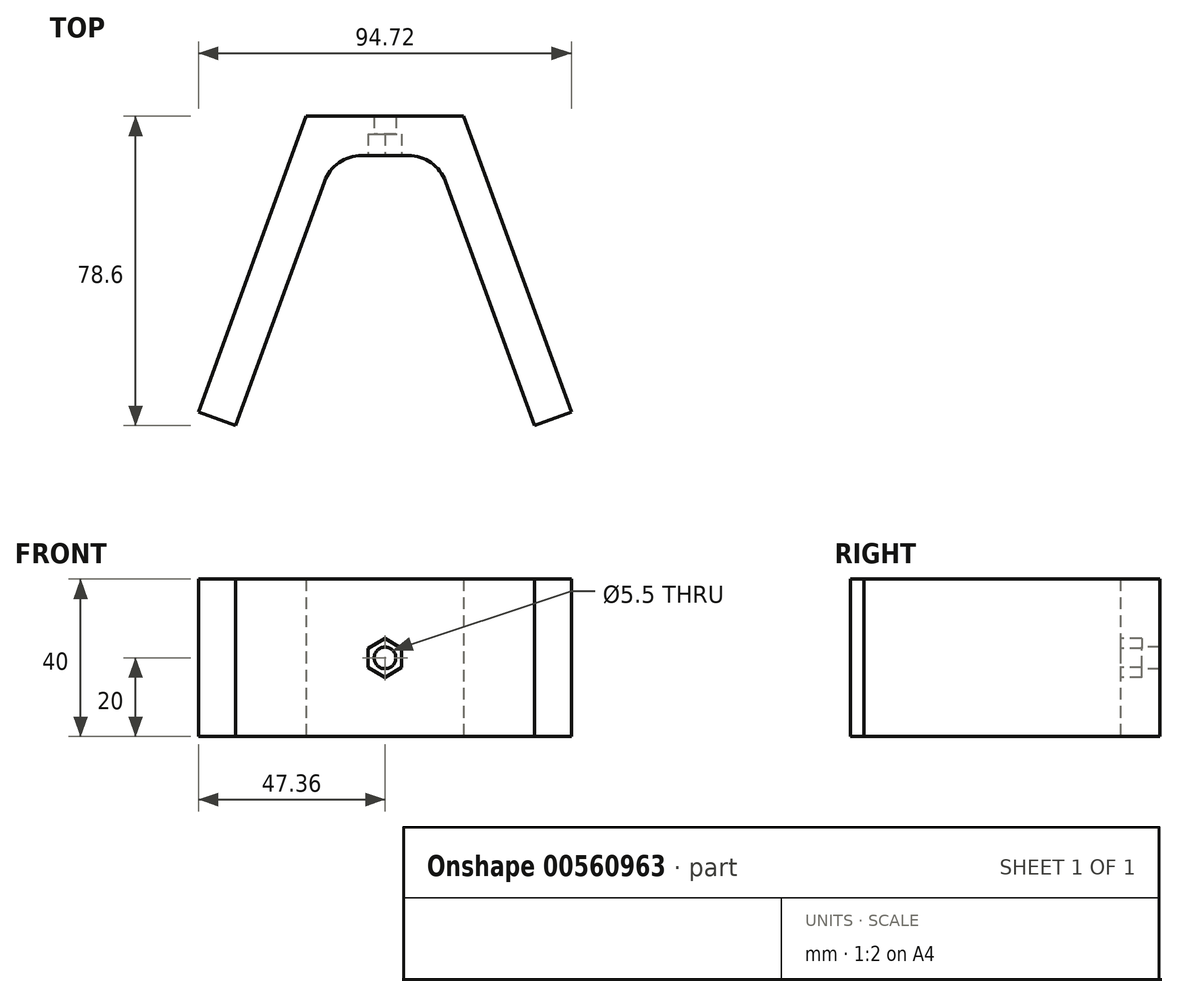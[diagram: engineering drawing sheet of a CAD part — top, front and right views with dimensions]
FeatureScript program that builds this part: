
annotation { "Feature Type Name" : "Feature", "Feature Type Description" : "" }
export const myFeature = defineFeature(function(context is Context, id is Id, definition is map)
    precondition{}
    {
        {
            var Q0;
            Q0=qCreatedBy(makeId("Top.planeOp"),FACE);
            var sketch = newSketch(context, id + "F0", { "sketchPlane" : qUnion([Q0])});
            skLineSegment(sketch, "E0.bottom", {"start": v(-20, 0) * mm, "end": v(0, 0) * mm});
            skLineSegment(sketch, "E0.top", {"start": v(-20, -10) * mm, "end": v(0, -10) * mm});
            skLineSegment(sketch, "E0.left", {"start": v(-20, 0) * mm, "end": v(-20, -10) * mm});
            skLineSegment(sketch, "E0.right", {"start": v(0, 0) * mm, "end": v(0, -10) * mm});
            skLineSegment(sketch, "E1", {"start": v(-20, 0) * mm, "end": v(-47.36, -75.18) * mm});
            skLineSegment(sketch, "E2", {"start": v(-47.36, -75.18) * mm, "end": v(-37.96, -78.6) * mm});
            skLineSegment(sketch, "E3", {"start": v(-37.96, -78.6) * mm, "end": v(-13, -10) * mm});
            skSolve(sketch);
        }
        {
            var Q0;
            Q0=makeQuery(id+"F0.imprint","IMPRINT",FACE,{"disambiguationData":[TD([[makeQuery(id+"F0.imprint","IMPRINT",EDGE,{"derivedFrom":sQuery(id+"F0.wireOp",EDGE,"E0.bottom")}),-1.0]])]});
            var Q1;
            {var subQ0=sQuery(id+"F0.wireOp",EDGE,"E0.left");Q1=makeQuery(id+"F0.imprint","IMPRINT",FACE,{"disambiguationData":[TD([[makeQuery(id+"F0.imprint","IMPRINT",EDGE,{"derivedFrom":subQ0}),-1.0]])]});}
            extrude(context, id + "F1", {"entities" : qUnion([Q0, Q1]), "depth" : 40 * mm, "offsetDistance" : 25 * mm});
        }
        {
            var Q0;
            Q0=makeQuery(id+"F1.opExtrude","SWEPT_BODY",BODY,{"disambiguationData":[OSD([sQuery(id+"F0.wireOp",EDGE,"E0.bottom"),sQuery(id+"F0.wireOp",EDGE,"E0.top"),sQuery(id+"F0.wireOp",EDGE,"E0.right"),sQuery(id+"F0.wireOp",EDGE,"E1"),sQuery(id+"F0.wireOp",EDGE,"E2"),sQuery(id+"F0.wireOp",EDGE,"E3")])]});
            var Q1;
            Q1=qCreatedBy(makeId("Right.planeOp"),FACE);
            mirror(context, id + "F2", {"operationType" : NewBodyOperationType.ADD, "entities" : qUnion([Q0]), "mirrorPlane" : qUnion([Q1])});
        }
        {
            var Q0;
            {var subQ0=makeQuery(id+"F1.opExtrude","SWEPT_FACE",FACE,{"disambiguationData":[OSD([sQuery(id+"F0.wireOp",EDGE,"E0.top")])]});Q0=makeQuery(id+"F2.boolean.opBoolean","MERGE",FACE,{"derivedFrom":[subQ0,makeQuery(id+"F2.opPattern","COPY",FACE,{"derivedFrom":subQ0,"instanceName":"1"})]});}
            var sketch = newSketch(context, id + "F3", { "sketchPlane" : qUnion([Q0])});
            skCircle(sketch, "E4", {"center": v(0, 20) * mm, "radius": 2.75 * mm});
            skPoint(sketch, "E4.centerSnap0", {"position": v(13, 20) * mm});
            skSolve(sketch);
        }
        {
            var Q0;
            Q0=makeQuery(id+"F3.imprint","IMPRINT",FACE,{"disambiguationData":[TD([[makeQuery(id+"F3.imprint","IMPRINT",EDGE,{"derivedFrom":sQuery(id+"F3.wireOp",EDGE,"E4")}),1.0]])]});
            extrude(context, id + "F4", {"entities" : qUnion([Q0]), "operationType" : NewBodyOperationType.REMOVE, "endBound" : BoundingType.UP_TO_NEXT, "oppositeDirection" : true, "depth" : 25 * mm, "offsetDistance" : 25 * mm});
        }
        {
            var Q0;
            {var subQ0=makeQuery(id+"F1.opExtrude","SWEPT_FACE",FACE,{"disambiguationData":[OSD([sQuery(id+"F0.wireOp",EDGE,"E0.top")])]});Q0=makeQuery(id+"F2.boolean.opBoolean","MERGE",FACE,{"derivedFrom":[subQ0,makeQuery(id+"F2.opPattern","COPY",FACE,{"derivedFrom":subQ0,"instanceName":"1"})]});}
            var sketch = newSketch(context, id + "F5", { "sketchPlane" : qUnion([Q0])});
            skCircle(sketch, "E5.cCircle", {"center": v(0, 20) * mm, "radius": 4.25 * mm, "construction": true});
            skLineSegment(sketch, "E5.0", {"start": v(0, 24.9) * mm, "end": v(4.25, 22.45) * mm});
            skLineSegment(sketch, "E5.1", {"start": v(4.25, 22.45) * mm, "end": v(4.25, 17.55) * mm});
            skLineSegment(sketch, "E5.2", {"start": v(4.25, 17.55) * mm, "end": v(0, 15.1) * mm});
            skLineSegment(sketch, "E5.3", {"start": v(0, 15.1) * mm, "end": v(-4.25, 17.55) * mm});
            skLineSegment(sketch, "E5.4", {"start": v(-4.25, 17.55) * mm, "end": v(-4.25, 22.45) * mm});
            skLineSegment(sketch, "E5.5", {"start": v(-4.25, 22.45) * mm, "end": v(0, 24.9) * mm});
            skPoint(sketch, "E5.0.midPoint", {"position": v(2.13, 23.68) * mm});
            skSolve(sketch);
        }
        {
            var Q0;
            Q0=makeQuery(id+"F5.imprint","IMPRINT",FACE,{"disambiguationData":[TD([[makeQuery(id+"F5.imprint","IMPRINT",EDGE,{"derivedFrom":sQuery(id+"F5.wireOp",EDGE,"E5.0")}),-1.0]])]});
            extrude(context, id + "F6", {"entities" : qUnion([Q0]), "operationType" : NewBodyOperationType.REMOVE, "oppositeDirection" : true, "depth" : 5.5 * mm, "offsetDistance" : 25 * mm});
        }
        {
            var Q0;
            Q0=makeQuery(id+"F1.opExtrude","SWEPT_EDGE",EDGE,{"disambiguationData":[OSD([sQuery(id+"F0.wireOp",EDGE,"E0.top"),sQuery(id+"F0.wireOp",EDGE,"E3")])]});
            var Q1;
            Q1=makeQuery(id+"F2.opPattern","COPY",EDGE,{"derivedFrom":makeQuery(id+"F1.opExtrude","SWEPT_EDGE",EDGE,{"disambiguationData":[OSD([sQuery(id+"F0.wireOp",EDGE,"E0.top"),sQuery(id+"F0.wireOp",EDGE,"E3")])]}),"instanceName":"1"});
            fillet(context, id + "F7", {"entities" : qUnion([Q0, Q1]), "radius" : 10 * mm, "tangentPropagation" : true, "allowEdgeOverflow" : false});
        }
    });
